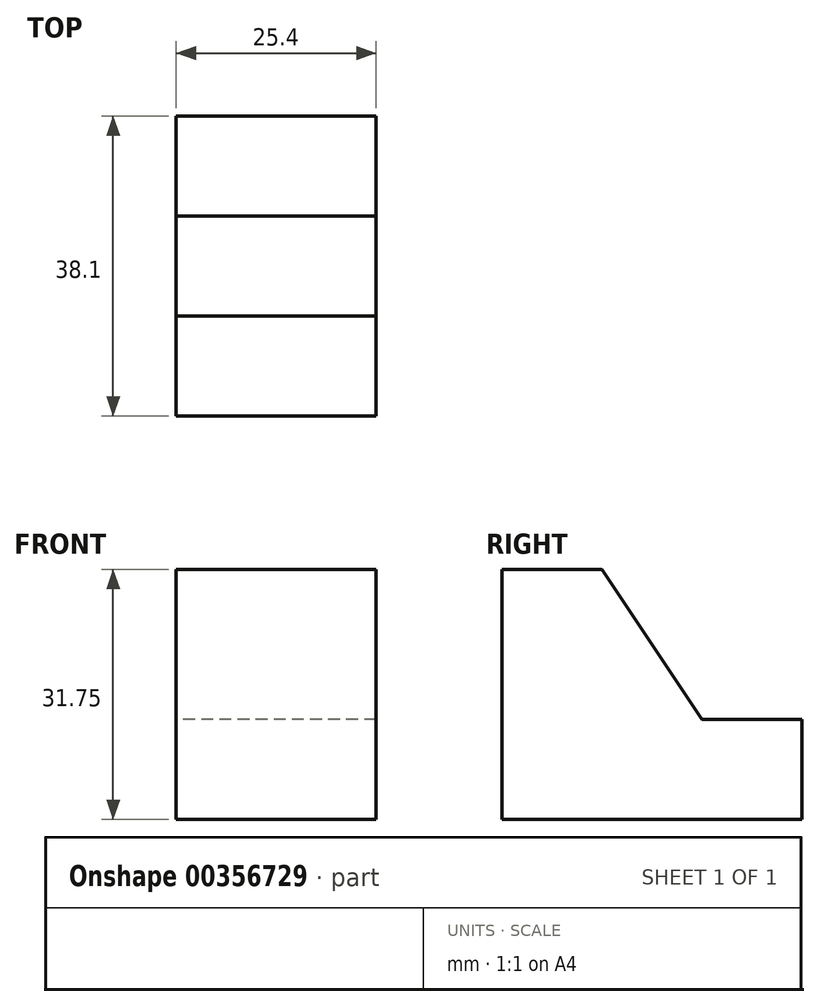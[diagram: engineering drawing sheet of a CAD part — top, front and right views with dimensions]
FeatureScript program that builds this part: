
annotation { "Feature Type Name" : "Feature", "Feature Type Description" : "" }
export const myFeature = defineFeature(function(context is Context, id is Id, definition is map)
    precondition{}
    {
        {
            var Q0;
            Q0=qCreatedBy(makeId("Right.planeOp"),FACE);
            var sketch = newSketch(context, id + "F0", { "sketchPlane" : qUnion([Q0])});
            skLineSegment(sketch, "E0", {"start": v(9.62, 0) * mm, "end": v(47.72, 0) * mm});
            skLineSegment(sketch, "E1", {"start": v(47.72, 0) * mm, "end": v(47.72, 12.7) * mm});
            skLineSegment(sketch, "E2", {"start": v(47.72, 12.7) * mm, "end": v(35.02, 12.7) * mm});
            skLineSegment(sketch, "E3", {"start": v(9.62, 0) * mm, "end": v(9.62, 31.75) * mm});
            skLineSegment(sketch, "E4", {"start": v(9.62, 31.75) * mm, "end": v(22.32, 31.75) * mm});
            skLineSegment(sketch, "E5", {"start": v(22.32, 31.75) * mm, "end": v(35.02, 12.7) * mm});
            skSolve(sketch);
        }
        {
            var Q0;
            Q0=makeQuery(id+"F0.imprint","IMPRINT",FACE,{"disambiguationData":[TD([[makeQuery(id+"F0.imprint","IMPRINT",EDGE,{"derivedFrom":sQuery(id+"F0.wireOp",EDGE,"E0")}),1.0]])]});
            extrude(context, id + "F1", {"entities" : qUnion([Q0]), "depth" : 25.4 * mm});
        }
    });
